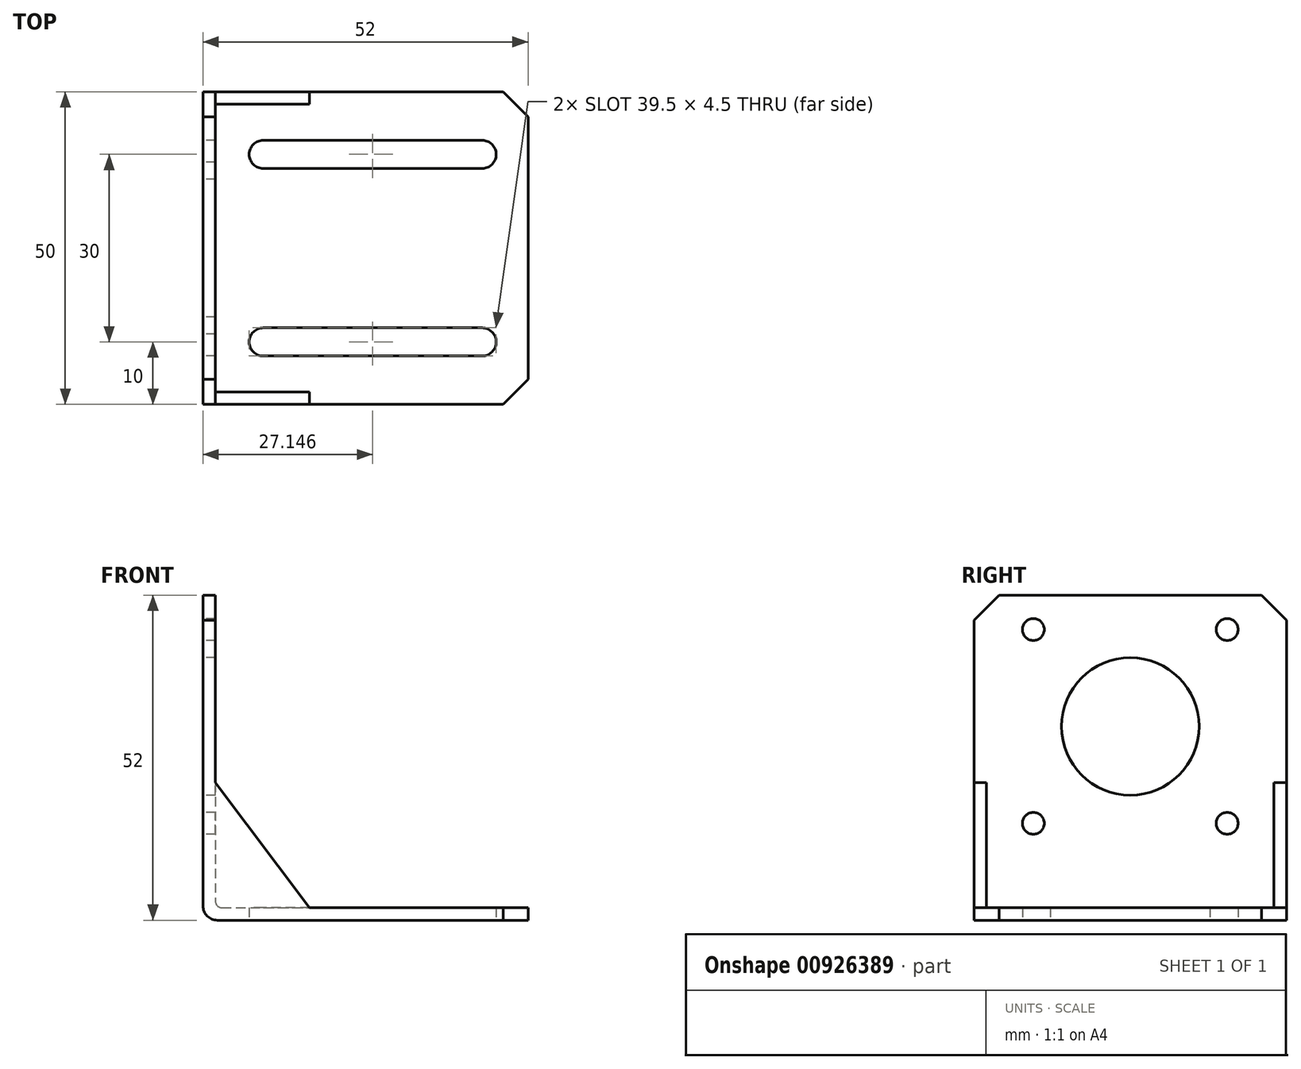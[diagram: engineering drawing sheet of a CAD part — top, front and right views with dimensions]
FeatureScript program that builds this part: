
annotation { "Feature Type Name" : "Feature", "Feature Type Description" : "" }
export const myFeature = defineFeature(function(context is Context, id is Id, definition is map)
    precondition{}
    {
        {
            var Q0;
            Q0=qCreatedBy(makeId("Front.planeOp"),FACE);
            var sketch = newSketch(context, id + "F0", { "sketchPlane" : qUnion([Q0])});
            skLineSegment(sketch, "E0", {"start": v(0, 52) * mm, "end": v(2, 52) * mm});
            skLineSegment(sketch, "E1", {"start": v(2, 52) * mm, "end": v(2, 3) * mm});
            skArc(sketch, "E2", {"start": v(2, 3) * mm, "mid": v(2.3, 2.3) * mm, "end": v(3, 2) * mm});
            skLineSegment(sketch, "E3", {"start": v(0, 52) * mm, "end": v(0, 2.3) * mm});
            skPoint(sketch, "E3.endSnap0", {"position": v(2.3, 2.3) * mm});
            skArc(sketch, "E4", {"start": v(0, 2.3) * mm, "mid": v(0.67, 0.67) * mm, "end": v(2.3, 0) * mm});
            skLineSegment(sketch, "E5", {"start": v(3, 2) * mm, "end": v(52, 2) * mm});
            skLineSegment(sketch, "E6", {"start": v(52, 2) * mm, "end": v(52, 0) * mm});
            skLineSegment(sketch, "E7", {"start": v(52, 0) * mm, "end": v(2.3, 0) * mm});
            skSolve(sketch);
        }
        {
            var Q0;
            Q0 = qSketchRegion(id + "F0", true);
            extrude(context, id + "F1", {"entities" : qUnion([Q0]), "depth" : 50 * mm, "offsetDistance" : 25 * mm});
        }
        {
            var Q0;
            Q0=makeQuery(id+"F1.opExtrude","CAP_FACE",FACE,{"disambiguationData":[OSD([sQuery(id+"F0.wireOp",EDGE,"E0"),sQuery(id+"F0.wireOp",EDGE,"E1"),sQuery(id+"F0.wireOp",EDGE,"E2"),sQuery(id+"F0.wireOp",EDGE,"E3"),sQuery(id+"F0.wireOp",EDGE,"E4"),sQuery(id+"F0.wireOp",EDGE,"E5"),sQuery(id+"F0.wireOp",EDGE,"E6"),sQuery(id+"F0.wireOp",EDGE,"E7")])],"isStart":false});
            var sketch = newSketch(context, id + "F2", { "sketchPlane" : qUnion([Q0])});
            skLineSegment(sketch, "E8", {"start": v(2, 22) * mm, "end": v(17, 2) * mm});
            skLineSegment(sketch, "E9", {"start": v(17, 2) * mm, "end": v(2, 2) * mm});
            skLineSegment(sketch, "E10", {"start": v(2, 2) * mm, "end": v(2, 22) * mm});
            skSolve(sketch);
        }
        {
            var Q0;
            Q0 = qSketchRegion(id + "F2", true);
            extrude(context, id + "F3", {"entities" : qUnion([Q0]), "operationType" : NewBodyOperationType.ADD, "oppositeDirection" : true, "depth" : 2 * mm, "offsetDistance" : 25 * mm});
        }
        {
            var Q0;
            Q0=makeQuery(id+"F1.opExtrude","CAP_FACE",FACE,{"disambiguationData":[OSD([sQuery(id+"F0.wireOp",EDGE,"E0"),sQuery(id+"F0.wireOp",EDGE,"E1"),sQuery(id+"F0.wireOp",EDGE,"E2"),sQuery(id+"F0.wireOp",EDGE,"E3"),sQuery(id+"F0.wireOp",EDGE,"E4"),sQuery(id+"F0.wireOp",EDGE,"E5"),sQuery(id+"F0.wireOp",EDGE,"E6"),sQuery(id+"F0.wireOp",EDGE,"E7")])],"isStart":true});
            var sketch = newSketch(context, id + "F4", { "sketchPlane" : qUnion([Q0])});
            skLineSegment(sketch, "E11", {"start": v(-2, 22) * mm, "end": v(-17, 2) * mm});
            skLineSegment(sketch, "E12", {"start": v(-17, 2) * mm, "end": v(-2, 2) * mm});
            skLineSegment(sketch, "E13", {"start": v(-2, 2) * mm, "end": v(-2, 22) * mm});
            skSolve(sketch);
        }
        {
            var Q0;
            Q0 = qSketchRegion(id + "F4", true);
            extrude(context, id + "F5", {"entities" : qUnion([Q0]), "operationType" : NewBodyOperationType.ADD, "oppositeDirection" : true, "depth" : 2 * mm, "offsetDistance" : 25 * mm});
        }
        {
            var Q0;
            Q0=makeQuery(id+"F1.opExtrude","SWEPT_FACE",FACE,{"disambiguationData":[OSD([sQuery(id+"F0.wireOp",EDGE,"E7")])]});
            var sketch = newSketch(context, id + "F6", { "sketchPlane" : qUnion([Q0])});
            skArc(sketch, "E14", {"start": v(44.65, 37.75) * mm, "mid": v(46.9, 40) * mm, "end": v(44.65, 42.25) * mm});
            skLineSegment(sketch, "E15", {"start": v(44.65, 37.75) * mm, "end": v(27.15, 37.75) * mm});
            skLineSegment(sketch, "E16", {"start": v(44.65, 42.25) * mm, "end": v(27.15, 42.25) * mm});
            skLineSegment(sketch, "E17", {"start": v(27.15, 50) * mm, "end": v(27.15, 0) * mm, "construction": true});
            skLineSegment(sketch, "E18", {"start": v(52, 25) * mm, "end": v(2.3, 25) * mm, "construction": true});
            skLineSegment(sketch, "E19.MirrorCS", {"start": v(9.65, 42.25) * mm, "end": v(27.15, 42.25) * mm});
            skArc(sketch, "E20.MirrorCS", {"start": v(9.65, 37.75) * mm, "mid": v(7.4, 40) * mm, "end": v(9.65, 42.25) * mm});
            skLineSegment(sketch, "E21.MirrorCS", {"start": v(9.65, 37.75) * mm, "end": v(27.15, 37.75) * mm});
            skLineSegment(sketch, "E22.MirrorCS", {"start": v(9.65, 12.25) * mm, "end": v(27.15, 12.25) * mm});
            skArc(sketch, "E23.MirrorCS", {"start": v(44.65, 12.25) * mm, "mid": v(46.9, 10) * mm, "end": v(44.65, 7.75) * mm});
            skArc(sketch, "E24.MirrorCS", {"start": v(9.65, 12.25) * mm, "mid": v(7.4, 10) * mm, "end": v(9.65, 7.75) * mm});
            skLineSegment(sketch, "E25.MirrorCS", {"start": v(9.65, 7.75) * mm, "end": v(27.15, 7.75) * mm});
            skLineSegment(sketch, "E26.MirrorCS", {"start": v(44.65, 7.75) * mm, "end": v(27.15, 7.75) * mm});
            skLineSegment(sketch, "E27.MirrorCS", {"start": v(44.65, 12.25) * mm, "end": v(27.15, 12.25) * mm});
            skSolve(sketch);
        }
        {
            var Q0;
            Q0 = qSketchRegion(id + "F6", true);
            extrude(context, id + "F7", {"entities" : qUnion([Q0]), "operationType" : NewBodyOperationType.REMOVE, "endBound" : BoundingType.THROUGH_ALL, "oppositeDirection" : true, "depth" : 25 * mm, "offsetDistance" : 25 * mm});
        }
        {
            var Q0;
            Q0=makeQuery(id+"F1.opExtrude","SWEPT_FACE",FACE,{"disambiguationData":[OSD([sQuery(id+"F0.wireOp",EDGE,"E3")])]});
            var sketch = newSketch(context, id + "F8", { "sketchPlane" : qUnion([Q0])});
            skCircle(sketch, "E28", {"center": v(25, 31) * mm, "radius": 11 * mm});
            skCircle(sketch, "E29", {"center": v(9.5, 46.5) * mm, "radius": 1.75 * mm});
            skCircle(sketch, "E30", {"center": v(9.5, 15.5) * mm, "radius": 1.75 * mm});
            skCircle(sketch, "E31", {"center": v(40.5, 15.5) * mm, "radius": 1.75 * mm});
            skCircle(sketch, "E32", {"center": v(40.5, 46.5) * mm, "radius": 1.75 * mm});
            skLineSegment(sketch, "E33", {"start": v(25, 52) * mm, "end": v(25, 2.3) * mm, "construction": true});
            skCircle(sketch, "E34", {"center": v(25, 31) * mm, "radius": 21.92 * mm, "construction": true});
            skLineSegment(sketch, "E35.bottom", {"start": v(9.5, 46.5) * mm, "end": v(40.5, 46.5) * mm, "construction": true});
            skLineSegment(sketch, "E35.top", {"start": v(9.5, 15.5) * mm, "end": v(40.5, 15.5) * mm, "construction": true});
            skLineSegment(sketch, "E35.left", {"start": v(9.5, 46.5) * mm, "end": v(9.5, 15.5) * mm, "construction": true});
            skLineSegment(sketch, "E35.right", {"start": v(40.5, 46.5) * mm, "end": v(40.5, 15.5) * mm, "construction": true});
            skSolve(sketch);
        }
        {
            var Q0;
            Q0 = qSketchRegion(id + "F8", true);
            extrude(context, id + "F9", {"entities" : qUnion([Q0]), "operationType" : NewBodyOperationType.REMOVE, "endBound" : BoundingType.THROUGH_ALL, "oppositeDirection" : true, "depth" : 25 * mm, "offsetDistance" : 25 * mm});
        }
        {
            var Q0;
            Q0=makeQuery(id+"F1.opExtrude","CAP_EDGE",EDGE,{"disambiguationData":[OSD([sQuery(id+"F0.wireOp",EDGE,"E0")])],"isStart":true});
            var Q1;
            Q1=makeQuery(id+"F1.opExtrude","CAP_EDGE",EDGE,{"disambiguationData":[OSD([sQuery(id+"F0.wireOp",EDGE,"E0")])],"isStart":false});
            var Q2;
            Q2=makeQuery(id+"F1.opExtrude","CAP_EDGE",EDGE,{"disambiguationData":[OSD([sQuery(id+"F0.wireOp",EDGE,"E6")])],"isStart":true});
            var Q3;
            Q3=makeQuery(id+"F1.opExtrude","CAP_EDGE",EDGE,{"disambiguationData":[OSD([sQuery(id+"F0.wireOp",EDGE,"E6")])],"isStart":false});
            chamfer(context, id + "F10", {"entities" : qUnion([Q0, Q1, Q2, Q3]), "width" : 4 * mm, "tangentPropagation" : true});
        }
    });
